# Revit family: Rohrschelle Omnia MB, M 8-M10, Silikon
name_source: partatom
category: HLS-Bauteile
revit_build: Autodesk Revit 2017 (Build: 20190507_1515(x64)
units: mm (PartAtom-declared; Revit-internal decimal feet)

## family parameters
Arbeitsebenenbasiert = Ja
Beim Laden mit Abzugskörper schneiden = Nein
Bemaßung runder Anschluss = Durchmesser verwenden
Gemeinsam genutzt = Ja
Immer vertikal = Nein
Raumberechnungspunkt = Nein
Teiletyp = Normal

## types (16) — shared parameters
Anschluss = M8/M10
BP = 14 mm  [stored 0.0459318 ft]
Bauart = zweiteilig
Baustoffklasse = B2
Brandschutz = RAL GZ 656
DS = 6 mm  [stored 0.019685 ft]
DVS = 5 mm  [stored 0.0164042 ft]
Dämmstärke = 6 mm  [stored 0.019685 ft]
Fabrikat = MEFA
Farbe Schalldämmeinlage = rot
Firma = MEFA Befestigungs- und Montagesysteme GmbH
HGA = 17 mm
L Ü Bogen = 19 mm  [stored 0.062336 ft]
Material = Stahl
Material Schalldämmeinlage = Silikon
Materialname = DD11
Mengeneinheit = St
Oberflaeche = galvanisch verzinkt
Schalldämmeinlage = Silikon
Verschluss = Schwenkbarer U-Verschluss
Verschluss-Schraube = M6
Vorgabe-Ansicht = 1219 mm
d1 = 7 mm  [stored 0.0229659 ft]
max. Temperaturbeständigkeit = 250 °C
max. zul. Last horizontal = 0.00 kN
max. zul. Last vertikal = 0.00 kN
zero-valued in all types: Nennweite DN Rohr, Rohraußendurchmesser, Stärke Material

## per-type parameters (varying)
- Omnia MB, Ø 15- 20, M8/M10, Silikon: A=25 mm  [stored 0.082021 ft]; AB=5 mm  [stored 0.0164042 ft]; Anschlußhöhe=24 mm; Artikelnummer=0398220; B=61 mm; Breite=61 mm; D=20 mm  [stored 0.0656168 ft]; D0=32 mm  [stored 0.104987 ft]; DF1=14 mm  [stored 0.0459318 ft]; DF2=12 mm  [stored 0.0393701 ft]; Dmax=20 mm  [stored 0.0656168 ft]; Dmin=15 mm  [stored 0.0492126 ft]; EAN=4250928408761; Gewicht=0.08 kg; Gewicht pro Bauteil=0.08 kg; H=52 mm; Kurztext1=Rohrschelle Omnia MB 20x1,5; Kurztext2=15 - 20 mm M8/M10 Silikon; MB=20 mm  [stored 0.0656168 ft]; MD=2 mm  [stored 0.00656168 ft]; Materialmaße=20x1,5 mm; R=16 mm  [stored 0.0524934 ft]; RM=18 mm  [stored 0.0590551 ft]; Rohraußendurchmesser Zoll=3/8 Zoll; S=47 mm  [stored 0.154199 ft]; S1=51 mm; max. Höhe=47 mm  [stored 0.154199 ft]; max. Rohraußendurchmesser=20 mm  [stored 0.0656168 ft]; max. zul. Last=1.00 kN; min. Rohraußendurchmesser=15 mm  [stored 0.0492126 ft]; vpe=100 St
- Omnia MB, Ø 22- 28, M8/M10, Silikon: A=25 mm  [stored 0.082021 ft]; AB=6 mm  [stored 0.019685 ft]; Anschlußhöhe=24 mm; Artikelnummer=0398228; B=69 mm; Breite=68 mm; D=28 mm  [stored 0.0918635 ft]; D0=40 mm  [stored 0.131234 ft]; DF1=14 mm  [stored 0.0459318 ft]; DF2=12 mm  [stored 0.0393701 ft]; Dmax=28 mm  [stored 0.0918635 ft]; Dmin=22 mm  [stored 0.0721785 ft]; EAN=4250928408778; Gewicht=0.09 kg; Gewicht pro Bauteil=0.09 kg; H=60 mm; Kurztext1=Rohrschelle Omnia MB 20x1,5; Kurztext2=22 - 28 mm M8/M10 Silikon; MB=20 mm  [stored 0.0656168 ft]; MD=2 mm  [stored 0.00656168 ft]; Materialmaße=20x1,5 mm; R=20 mm  [stored 0.0656168 ft]; RM=22 mm  [stored 0.0721785 ft]; Rohraußendurchmesser Zoll=1/2-3/4 Zoll; S=55 mm; S1=59 mm; max. Höhe=56 mm; max. Rohraußendurchmesser=28 mm  [stored 0.0918635 ft]; max. zul. Last=1.00 kN; min. Rohraußendurchmesser=22 mm  [stored 0.0721785 ft]; vpe=100 St
- Omnia MB, Ø 38- 42, M8/M10, Silikon: A=25 mm  [stored 0.082021 ft]; AB=4 mm  [stored 0.0131234 ft]; Anschlußhöhe=24 mm; Artikelnummer=0398242; B=88 mm; Breite=89 mm; D=42 mm  [stored 0.137795 ft]; D0=54 mm; DF1=16 mm  [stored 0.0524934 ft]; DF2=14 mm  [stored 0.0459318 ft]; Dmax=42 mm  [stored 0.137795 ft]; Dmin=38 mm  [stored 0.124672 ft]; EAN=4250928408792; Gewicht=0.12 kg; Gewicht pro Bauteil=0.12 kg; H=75 mm; Kurztext1=Rohrschelle Omnia MB 20x2,0; Kurztext2=38 - 42 mm M8/M10 Silikon; MB=20 mm  [stored 0.0656168 ft]; MD=2 mm  [stored 0.00656168 ft]; Materialmaße=20x2,0 mm; R=27 mm; RM=29 mm; Rohraußendurchmesser Zoll=1 1/4 Zoll; S=72 mm; S1=73 mm; max. Höhe=70 mm; max. Rohraußendurchmesser=42 mm  [stored 0.137795 ft]; max. zul. Last=1.60 kN; min. Rohraußendurchmesser=38 mm  [stored 0.124672 ft]; vpe=50 St
- Omnia MB, Ø 30- 35, M8/M10, Silikon: A=25 mm  [stored 0.082021 ft]; AB=5 mm  [stored 0.0164042 ft]; Anschlußhöhe=24 mm; Artikelnummer=0398235; B=78 mm; Breite=78 mm; D=35 mm  [stored 0.114829 ft]; D0=47 mm  [stored 0.154199 ft]; DF1=14 mm  [stored 0.0459318 ft]; DF2=14 mm  [stored 0.0459318 ft]; Dmax=35 mm  [stored 0.114829 ft]; Dmin=30 mm  [stored 0.0984252 ft]; EAN=4250928408785; Gewicht=0.10 kg; Gewicht pro Bauteil=0.10 kg; H=67 mm; Kurztext1=Rohrschelle Omnia MB 20x1,5; Kurztext2=30 - 35 mm M8/M10 Silikon; MB=20 mm  [stored 0.0656168 ft]; MD=2 mm  [stored 0.00656168 ft]; Materialmaße=20x1,5 mm; R=24 mm  [stored 0.0787402 ft]; RM=25 mm  [stored 0.082021 ft]; Rohraußendurchmesser Zoll=1 Zoll; S=64 mm; S1=66 mm; max. Höhe=62 mm; max. Rohraußendurchmesser=35 mm  [stored 0.114829 ft]; max. zul. Last=1.00 kN; min. Rohraußendurchmesser=30 mm  [stored 0.0984252 ft]; vpe=100 St
- Omnia MB, Ø 44- 48, M8/M10, Silikon: A=25 mm  [stored 0.082021 ft]; AB=4 mm  [stored 0.0131234 ft]; Anschlußhöhe=24 mm; Artikelnummer=0398248; B=92 mm; Breite=92 mm; D=48 mm  [stored 0.15748 ft]; D0=60 mm; DF1=14 mm  [stored 0.0459318 ft]; DF2=14 mm  [stored 0.0459318 ft]; Dmax=48 mm  [stored 0.15748 ft]; Dmin=44 mm  [stored 0.144357 ft]; EAN=4250928408808; Gewicht=0.13 kg; Gewicht pro Bauteil=0.13 kg; H=81 mm; Kurztext1=Rohrschelle Omnia MB 20x2,0; Kurztext2=44 - 48 mm M8/M10 Silikon; MB=20 mm  [stored 0.0656168 ft]; MD=2 mm  [stored 0.00656168 ft]; Materialmaße=20x2,0 mm; R=30 mm  [stored 0.0984252 ft]; RM=32 mm  [stored 0.104987 ft]; Rohraußendurchmesser Zoll=1 1/2 Zoll; S=78 mm; S1=79 mm; max. Höhe=76 mm; max. Rohraußendurchmesser=48 mm  [stored 0.15748 ft]; max. zul. Last=1.60 kN; min. Rohraußendurchmesser=44 mm  [stored 0.144357 ft]; vpe=50 St
- Omnia MB, Ø 50- 54, M8/M10, Silikon: A=25 mm  [stored 0.082021 ft]; AB=4 mm  [stored 0.0131234 ft]; Anschlußhöhe=24 mm; Artikelnummer=0398254; B=101 mm; Breite=101 mm; D=54 mm; D0=66 mm; DF1=15 mm  [stored 0.0492126 ft]; DF2=16 mm  [stored 0.0524934 ft]; Dmax=54 mm; Dmin=50 mm  [stored 0.164042 ft]; EAN=4250928408815; Gewicht=0.14 kg; Gewicht pro Bauteil=0.14 kg; H=87 mm; Kurztext1=Rohrschelle Omnia MB 20x2,0; Kurztext2=50 - 54 mm M8/M10 Silikon; MB=20 mm  [stored 0.0656168 ft]; MD=2 mm  [stored 0.00656168 ft]; Materialmaße=20x2,0 mm; R=33 mm  [stored 0.108268 ft]; RM=35 mm  [stored 0.114829 ft]; Rohraußendurchmesser Zoll=Zoll; S=86 mm; S1=85 mm; max. Höhe=82 mm; max. Rohraußendurchmesser=54 mm; max. zul. Last=1.60 kN; min. Rohraußendurchmesser=50 mm  [stored 0.164042 ft]; vpe=50 St
- Omnia MB, Ø 56- 60, M8/M10, Silikon: A=25 mm  [stored 0.082021 ft]; AB=4 mm  [stored 0.0131234 ft]; Anschlußhöhe=24 mm; Artikelnummer=0398260; B=108 mm; Breite=108 mm; D=60 mm; D0=72 mm; DF1=16 mm  [stored 0.0524934 ft]; DF2=16 mm  [stored 0.0524934 ft]; Dmax=60 mm; Dmin=56 mm; EAN=4250928408822; Gewicht=0.15 kg; Gewicht pro Bauteil=0.15 kg; H=93 mm; Kurztext1=Rohrschelle Omnia MB 20x2,0; Kurztext2=56 - 60 mm M8/M10 Silikon; MB=20 mm  [stored 0.0656168 ft]; MD=2 mm  [stored 0.00656168 ft]; Materialmaße=20x2,0 mm; R=36 mm; RM=38 mm  [stored 0.124672 ft]; Rohraußendurchmesser Zoll=2 Zoll; S=92 mm; S1=91 mm; max. Höhe=88 mm; max. Rohraußendurchmesser=60 mm; max. zul. Last=1.60 kN; min. Rohraußendurchmesser=56 mm; vpe=50 St
- Omnia MB, Ø 61- 65, M8/M10, Silikon: A=25 mm  [stored 0.082021 ft]; AB=4 mm  [stored 0.0131234 ft]; Anschlußhöhe=24 mm; Artikelnummer=0398264; B=113 mm; Breite=113 mm; D=65 mm; D0=77 mm; DF1=16 mm  [stored 0.0524934 ft]; DF2=16 mm  [stored 0.0524934 ft]; Dmax=65 mm; Dmin=61 mm; EAN=4250928408839; Gewicht=0.15 kg; Gewicht pro Bauteil=0.15 kg; H=98 mm; Kurztext1=Rohrschelle Omnia MB 20x2,0; Kurztext2=61 - 65 mm M8/M10 Silikon; MB=20 mm  [stored 0.0656168 ft]; MD=2 mm  [stored 0.00656168 ft]; Materialmaße=20x2,0 mm; R=39 mm; RM=41 mm; Rohraußendurchmesser Zoll=Zoll; S=97 mm; S1=96 mm; max. Höhe=92 mm; max. Rohraußendurchmesser=65 mm; max. zul. Last=1.60 kN; min. Rohraußendurchmesser=61 mm; vpe=50 St
- Omnia MB, Ø 70- 73, M8/M10, Silikon: A=25 mm  [stored 0.082021 ft]; AB=3 mm  [stored 0.00984252 ft]; Anschlußhöhe=24 mm; Artikelnummer=0398273; B=117 mm; Breite=117 mm; D=73 mm; D0=85 mm; DF1=14 mm  [stored 0.0459318 ft]; DF2=14 mm  [stored 0.0459318 ft]; Dmax=73 mm; Dmin=70 mm; EAN=4250928408846; Gewicht=0.17 kg; Gewicht pro Bauteil=0.17 kg; H=106 mm; Kurztext1=Rohrschelle Omnia MB 20x2,0; Kurztext2=70 - 73 mm M8/M10 Silikon; MB=20 mm  [stored 0.0656168 ft]; MD=2 mm  [stored 0.00656168 ft]; Materialmaße=20x2,0 mm; R=43 mm; RM=45 mm; Rohraußendurchmesser Zoll=Zoll; S=103 mm; S1=104 mm; max. Höhe=101 mm; max. Rohraußendurchmesser=73 mm; max. zul. Last=1.60 kN; min. Rohraußendurchmesser=70 mm; vpe=50 St
- Omnia MB, Ø 75- 83, M8/M10, Silikon: A=25 mm  [stored 0.082021 ft]; AB=8 mm  [stored 0.0262467 ft]; Anschlußhöhe=24 mm; Artikelnummer=0398278; B=124 mm; Breite=124 mm; D=83 mm; D0=95 mm; DF1=12 mm  [stored 0.0393701 ft]; DF2=13 mm; Dmax=83 mm; Dmin=75 mm; EAN=4250928408853; Gewicht=0.18 kg; Gewicht pro Bauteil=0.18 kg; H=116 mm; Kurztext1=Rohrschelle Omnia MB 20x2,0; Kurztext2=75 - 83 mm M8/M10 Silikon; MB=20 mm  [stored 0.0656168 ft]; MD=2 mm  [stored 0.00656168 ft]; Materialmaße=20x2,0 mm; R=48 mm  [stored 0.15748 ft]; RM=50 mm  [stored 0.164042 ft]; Rohraußendurchmesser Zoll=2 1/2 Zoll; S=112 mm; S1=114 mm; max. Höhe=108 mm; max. Rohraußendurchmesser=83 mm; max. zul. Last=1.60 kN; min. Rohraußendurchmesser=75 mm; vpe=50 St
- Omnia MB, Ø 84- 89, M8/M10, Silikon: A=26 mm; AB=5 mm  [stored 0.0164042 ft]; Anschlußhöhe=25 mm; Artikelnummer=0398289; B=136 mm; Breite=136 mm; D=89 mm; D0=101 mm; DF1=15 mm  [stored 0.0492126 ft]; DF2=15 mm  [stored 0.0492126 ft]; Dmax=89 mm; Dmin=84 mm; EAN=4250928408860; Gewicht=0.26 kg; Gewicht pro Bauteil=0.26 kg; H=123 mm; Kurztext1=Rohrschelle Omnia MB 25x2,5; Kurztext2=84 - 89 mm M8/M10 Silikon; MB=25 mm  [stored 0.082021 ft]; MD=3 mm  [stored 0.00984252 ft]; Materialmaße=25x2,5 mm; R=51 mm; RM=53 mm; Rohraußendurchmesser Zoll=3 Zoll; S=121 mm; S1=120 mm; max. Höhe=118 mm; max. Rohraußendurchmesser=89 mm; max. zul. Last=1.80 kN; min. Rohraußendurchmesser=84 mm; vpe=50 St
- Omnia MB, Ø 90- 95, M8/M10, Silikon: A=26 mm; AB=5 mm  [stored 0.0164042 ft]; Anschlußhöhe=25 mm; Artikelnummer=0398295; B=143 mm; Breite=143 mm; D=95 mm; D0=107 mm; DF1=16 mm  [stored 0.0524934 ft]; DF2=15 mm  [stored 0.0492126 ft]; Dmax=95 mm; Dmin=90 mm; EAN=4250928408877; Gewicht=0.27 kg; Gewicht pro Bauteil=0.27 kg; H=129 mm; Kurztext1=Rohrschelle Omnia MB 25x2,5; Kurztext2=90 - 95 mm M8/M10 Silikon; MB=25 mm  [stored 0.082021 ft]; MD=3 mm  [stored 0.00984252 ft]; Materialmaße=25x2,5 mm; R=54 mm; RM=56 mm; Rohraußendurchmesser Zoll=Zoll; S=127 mm; S1=126 mm; max. Höhe=124 mm; max. Rohraußendurchmesser=95 mm; max. zul. Last=1.80 kN; min. Rohraußendurchmesser=90 mm; vpe=50 St
- Omnia MB, Ø100-105, M8/M10, Silikon: A=26 mm; AB=5 mm  [stored 0.0164042 ft]; Anschlußhöhe=25 mm; Artikelnummer=0398305; B=152 mm; Breite=152 mm; D=105 mm; D0=117 mm; DF1=15 mm  [stored 0.0492126 ft]; DF2=15 mm  [stored 0.0492126 ft]; Dmax=105 mm; Dmin=100 mm; EAN=4250928408884; Gewicht=0.29 kg; Gewicht pro Bauteil=0.29 kg; H=139 mm; Kurztext1=Rohrschelle Omnia MB 25x2,5; Kurztext2=100 - 105 mm M8/M10 Silikon; MB=25 mm  [stored 0.082021 ft]; MD=3 mm  [stored 0.00984252 ft]; Materialmaße=25x2,5 mm; R=59 mm; RM=61 mm; Rohraußendurchmesser Zoll=Zoll; S=137 mm; S1=136 mm; max. Höhe=134 mm; max. Rohraußendurchmesser=105 mm; max. zul. Last=1.80 kN; min. Rohraußendurchmesser=100 mm; vpe=50 St
- Omnia MB, Ø108-112, M8/M10, Silikon: A=26 mm; AB=4 mm  [stored 0.0131234 ft]; Anschlußhöhe=25 mm; Artikelnummer=0398312; B=158 mm; Breite=158 mm; D=112 mm; D0=124 mm; DF1=15 mm  [stored 0.0492126 ft]; DF2=14 mm  [stored 0.0459318 ft]; Dmax=112 mm; Dmin=108 mm; EAN=4250928408891; Gewicht=0.30 kg; Gewicht pro Bauteil=0.30 kg; H=146 mm; Kurztext1=Rohrschelle Omnia MB 25x2,5; Kurztext2=108 - 112 mm M8/M10 Silikon; MB=25 mm  [stored 0.082021 ft]; MD=3 mm  [stored 0.00984252 ft]; Materialmaße=25x2,5 mm; R=62 mm; RM=65 mm; Rohraußendurchmesser Zoll=Zoll; S=143 mm; S1=143 mm; max. Höhe=141 mm; max. Rohraußendurchmesser=112 mm; max. zul. Last=1.80 kN; min. Rohraußendurchmesser=108 mm; vpe=50 St
- Omnia MB, Ø114-116, M8/M10, Silikon: A=26 mm; AB=2 mm  [stored 0.00656168 ft]; Anschlußhöhe=25 mm; Artikelnummer=0398316; B=165 mm; Breite=165 mm; D=116 mm; D0=128 mm; DF1=16 mm  [stored 0.0524934 ft]; DF2=16 mm  [stored 0.0524934 ft]; Dmax=116 mm; Dmin=114 mm; EAN=4250928408907; Gewicht=0.32 kg; Gewicht pro Bauteil=0.32 kg; H=150 mm; Kurztext1=Rohrschelle Omnia MB 25x2,5; Kurztext2=114 - 116 mm M8/M10 Silikon; MB=25 mm  [stored 0.082021 ft]; MD=3 mm  [stored 0.00984252 ft]; Materialmaße=25x2,5 mm; R=64 mm; RM=67 mm; Rohraußendurchmesser Zoll=4 Zoll; S=149 mm; S1=147 mm; max. Höhe=145 mm; max. Rohraußendurchmesser=116 mm; max. zul. Last=1.80 kN; min. Rohraußendurchmesser=114 mm; vpe=50 St
- Omnia MB, Ø121-125, M8/M10, Silikon: A=26 mm; AB=4 mm  [stored 0.0131234 ft]; Anschlußhöhe=25 mm; Artikelnummer=0398325; B=175 mm; Breite=175 mm; D=125 mm; D0=137 mm; DF1=17 mm; DF2=16 mm  [stored 0.0524934 ft]; Dmax=125 mm; Dmin=121 mm; EAN=4250928408914; Gewicht=0.33 kg; Gewicht pro Bauteil=0.33 kg; H=159 mm; Kurztext1=Rohrschelle Omnia MB 25x2,5; Kurztext2=121 - 125 mm M8/M10 Silikon; MB=25 mm  [stored 0.082021 ft]; MD=3 mm  [stored 0.00984252 ft]; Materialmaße=25x2,5 mm; R=69 mm; RM=71 mm; Rohraußendurchmesser Zoll=Zoll; S=158 mm; S1=156 mm; max. Höhe=154 mm; max. Rohraußendurchmesser=125 mm; max. zul. Last=1.80 kN; min. Rohraußendurchmesser=121 mm; vpe=25 St

note: [stored X ft] marks values corroborated as IEEE doubles in the binary element streams (Revit-internal decimal feet)

## geometry (parser evidence)
native form markers: Sweep x2
no freeform markers — native parametric forms only
